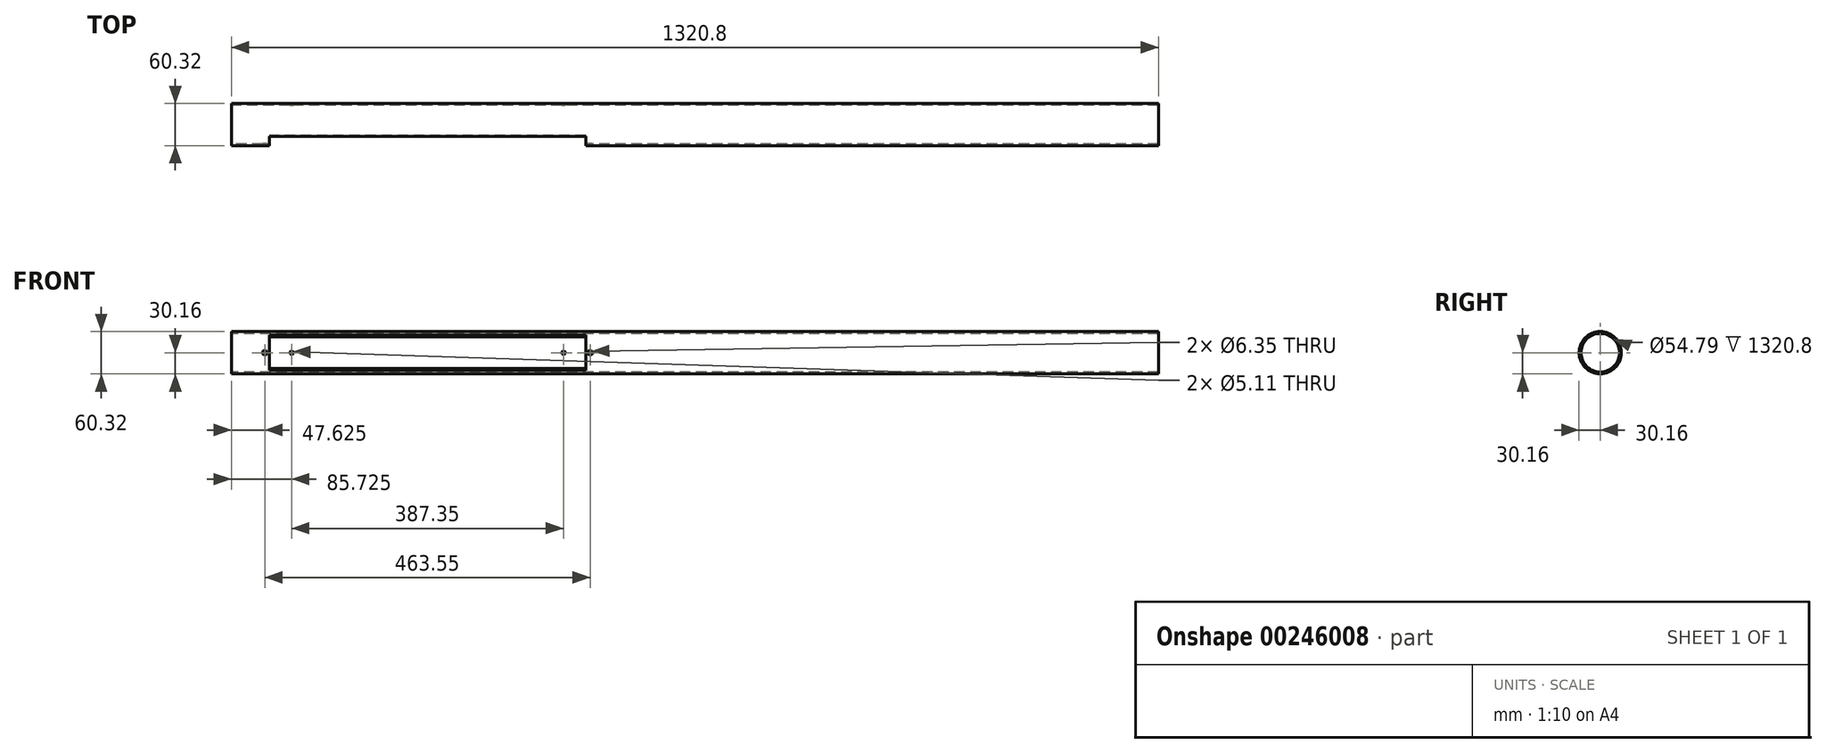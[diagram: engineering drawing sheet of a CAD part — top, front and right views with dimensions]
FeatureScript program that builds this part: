
annotation { "Feature Type Name" : "Feature", "Feature Type Description" : "" }
export const myFeature = defineFeature(function(context is Context, id is Id, definition is map)
    precondition{}
    {
        {
            var Q0;
            Q0=qCreatedBy(makeId("Right.planeOp"),FACE);
            var sketch = newSketch(context, id + "F0", { "sketchPlane" : qUnion([Q0])});
            skCircle(sketch, "E0", {"center": v(0, 0) * mm, "radius": 30.16 * mm});
            skCircle(sketch, "E1.0", {"center": v(0, 0) * mm, "radius": 27.4 * mm});
            skSolve(sketch);
        }
        {
            var Q0;
            Q0 = qSketchRegion(id + "F0", true);
            extrude(context, id + "F1", {"entities" : qUnion([Q0]), "depth" : 1320.8 * mm});
        }
        {
            var Q0;
            Q0=makeQuery(id+"F1.opExtrude","CAP_FACE",FACE,{"disambiguationData":[OSD([sQuery(id+"F0.wireOp",EDGE,"E0"),sQuery(id+"F0.wireOp",EDGE,"E1.0")])],"isStart":true});
            cPlane(context, id + "F2", {"entities" : qUnion([Q0]), "cplaneType" : CPlaneType.OFFSET, "offset" : 53.97 * mm, "oppositeDirection" : true, "width" : 152.4 * mm, "height" : 152.4 * mm});
        }
        {
            var Q0;
            Q0=qCreatedBy(id+"F2.planeOp",FACE);
            var sketch = newSketch(context, id + "F3", { "sketchPlane" : qUnion([Q0])});
            skLineSegment(sketch, "E2", {"start": v(0, 0) * mm, "end": v(35.9, 0) * mm});
            skLineSegment(sketch, "E3", {"start": v(0, 0) * mm, "end": v(28.73, 42.28) * mm});
            skLineSegment(sketch, "E4", {"start": v(0, 0) * mm, "end": v(28.45, -41.88) * mm});
            skLineSegment(sketch, "E5", {"start": v(28.73, 42.28) * mm, "end": v(35.9, 0) * mm});
            skLineSegment(sketch, "E6", {"start": v(35.9, 0) * mm, "end": v(28.45, -41.88) * mm});
            skSolve(sketch);
        }
        {
            var Q0;
            Q0 = qSketchRegion(id + "F3", true);
            extrude(context, id + "F4", {"entities" : qUnion([Q0]), "operationType" : NewBodyOperationType.REMOVE, "oppositeDirection" : true, "depth" : 450.85 * mm});
        }
        {
            var Q0;
            Q0=qCreatedBy(makeId("Front.planeOp"),FACE);
            var sketch = newSketch(context, id + "F5", { "sketchPlane" : qUnion([Q0])});
            skCircle(sketch, "E7", {"center": v(47.62, 0) * mm, "radius": 3.18 * mm});
            skCircle(sketch, "E8", {"center": v(511.18, 0) * mm, "radius": 3.18 * mm});
            skSolve(sketch);
        }
        {
            var Q0;
            Q0 = qSketchRegion(id + "F5", true);
            extrude(context, id + "F6", {"entities" : qUnion([Q0]), "operationType" : NewBodyOperationType.REMOVE, "depth" : 76.2 * mm});
        }
        {
            var Q0;
            Q0=qCreatedBy(makeId("Front.planeOp"),FACE);
            var sketch = newSketch(context, id + "F7", { "sketchPlane" : qUnion([Q0])});
            skCircle(sketch, "E9", {"center": v(85.73, 0) * mm, "radius": 2.55 * mm});
            skCircle(sketch, "E10", {"center": v(473.08, 0) * mm, "radius": 2.55 * mm});
            skSolve(sketch);
        }
        {
            var Q0;
            Q0 = qSketchRegion(id + "F7", true);
            extrude(context, id + "F8", {"entities" : qUnion([Q0]), "operationType" : NewBodyOperationType.REMOVE, "oppositeDirection" : true, "depth" : 76.2 * mm});
        }
    });
